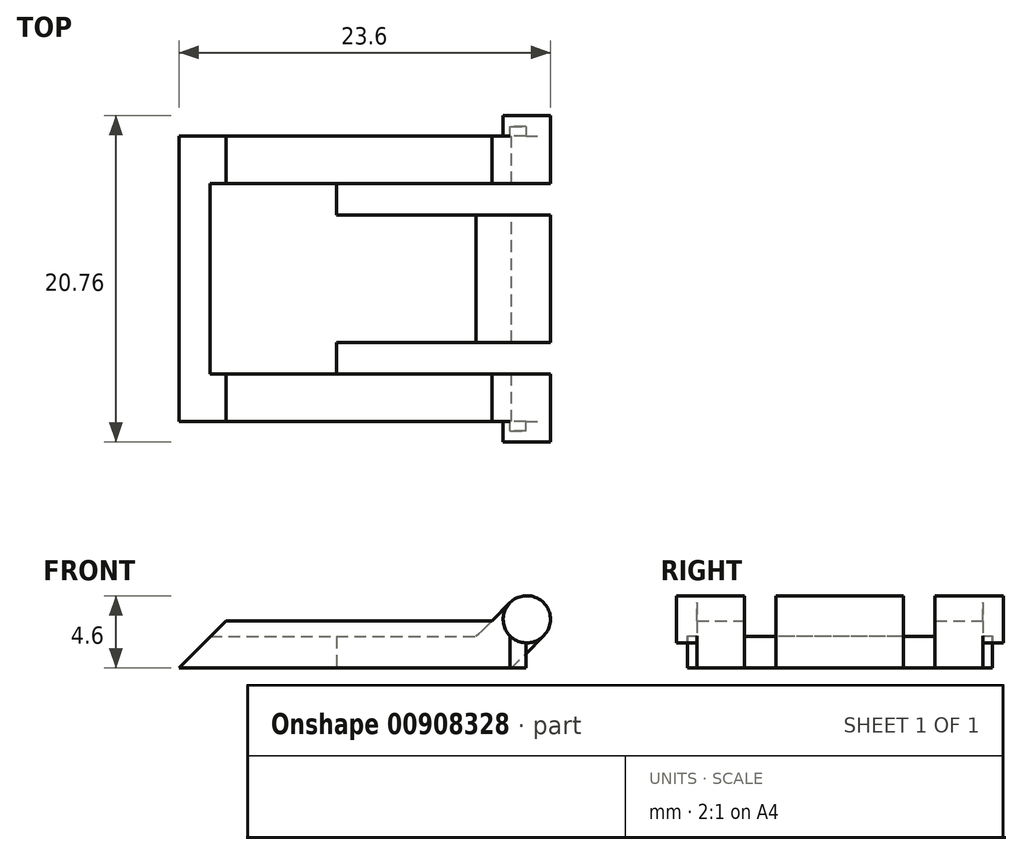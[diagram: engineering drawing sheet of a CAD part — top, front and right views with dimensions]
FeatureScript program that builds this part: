
annotation { "Feature Type Name" : "Feature", "Feature Type Description" : "" }
export const myFeature = defineFeature(function(context is Context, id is Id, definition is map)
    precondition{}
    {
        {
            var Q0;
            Q0=qCreatedBy(makeId("Front.planeOp"),FACE);
            var sketch = newSketch(context, id + "F0", { "sketchPlane" : qUnion([Q0])});
            skLineSegment(sketch, "E0", {"start": v(-6.08, 0) * mm, "end": v(15.04, 0) * mm});
            skLineSegment(sketch, "E1", {"start": v(-3.08, 3) * mm, "end": v(-6.08, 0) * mm});
            skLineSegment(sketch, "E2.trimOffspring", {"start": v(13.8, 3) * mm, "end": v(-3.08, 3) * mm});
            skArc(sketch, "E3", {"start": v(17.08, 2.04) * mm, "mid": v(17.08, 4.16) * mm, "end": v(14.96, 4.16) * mm});
            skLineSegment(sketch, "E4", {"start": v(15.04, 0) * mm, "end": v(17.08, 2.04) * mm});
            skLineSegment(sketch, "E5", {"start": v(13.8, 3) * mm, "end": v(14.96, 4.16) * mm});
            skSolve(sketch);
        }
        {
            var Q0;
            Q0 = qSketchRegion(id + "F0", true);
            extrude(context, id + "F1", {"entities" : qUnion([Q0]), "endBound" : BoundingType.SYMMETRIC, "depth" : 18.15 * mm, "offsetDistance" : 25 * mm});
        }
        {
            var Q0;
            Q0=makeQuery(id+"F1.opExtrude","CAP_FACE",FACE,{"disambiguationData":[OSD([sQuery(id+"F0.wireOp",EDGE,"E0"),sQuery(id+"F0.wireOp",EDGE,"IyzmLPVo-ZiIU-ZuMi-H74O-UJ5JQLBCPmE3"),sQuery(id+"F0.wireOp",EDGE,"E1"),sQuery(id+"F0.wireOp",EDGE,"0OPfdOSm-VN7Y-lchg-oPGg-Y34SgASty5nC"),sQuery(id+"F0.wireOp",EDGE,"E2.trimOffspring")])],"isStart":false});
            var sketch = newSketch(context, id + "F2", { "sketchPlane" : qUnion([Q0])});
            skCircle(sketch, "E6", {"center": v(16.02, 3.1) * mm, "radius": 1.5 * mm});
            skSolve(sketch);
        }
        {
            var Q0;
            {var subQ0=sQuery(id+"F2.wireOp",EDGE,"E6");var subQ1=makeQuery(id+"F2.imprint","INTERSECT",VERTEX,{"derivedFrom":[makeQuery(id+"F1.opExtrude","CAP_EDGE",EDGE,{"disambiguationData":[OSD([sQuery(id+"F0.wireOp",EDGE,"IyzmLPVo-ZiIU-ZuMi-H74O-UJ5JQLBCPmE3")])],"isStart":false}),subQ0]});Q0=makeQuery(id+"F2.imprint","IMPRINT",FACE,{"disambiguationData":[TD([[makeQuery(id+"F2.imprint","IMPRINT",EDGE,{"disambiguationData":[TD([[subQ1,-1.0]])],"derivedFrom":subQ0}),1.0]])]});}
            var Q1;
            Q1=sQuery(id+"F2.wireOp",EDGE,"E6");
            extrude(context, id + "F3", {"entities" : qUnion([Q0]), "surfaceEntities" : qUnion([Q1]), "depth" : 1.3 * mm, "offsetDistance" : 25 * mm});
        }
        {
            var Q0;
            Q0=makeQuery(id+"F3.opExtrude","SWEPT_BODY",BODY,{"disambiguationData":[OSD([sQuery(id+"F2.wireOp",EDGE,"E6")])]});
            var Q1;
            Q1=qCreatedBy(makeId("Front.planeOp"),FACE);
            mirror(context, id + "F4", {"operationType" : NewBodyOperationType.ADD, "entities" : qUnion([Q0]), "mirrorPlane" : qUnion([Q1])});
        }
        {
            var Q0;
            Q0=qCreatedBy(makeId("Front.planeOp"),FACE);
            var sketch = newSketch(context, id + "F5", { "sketchPlane" : qUnion([Q0])});
            skLineSegment(sketch, "E7.0", {"start": v(13.8, 3) * mm, "end": v(-3.08, 3) * mm});
            skLineSegment(sketch, "E7.2", {"start": v(-3.08, 3) * mm, "end": v(-4.08, 2) * mm});
            skLineSegment(sketch, "E8", {"start": v(-4.08, 2) * mm, "end": v(12.8, 2) * mm});
            skLineSegment(sketch, "E9", {"start": v(12.8, 2) * mm, "end": v(13.8, 3) * mm});
            skPoint(sketch, "E10.orphan", {"position": v(-6.08, 0) * mm});
            skSolve(sketch);
        }
        {
            var Q0;
            Q0 = qSketchRegion(id + "F5", true);
            extrude(context, id + "F6", {"entities" : qUnion([Q0]), "operationType" : NewBodyOperationType.REMOVE, "endBound" : BoundingType.SYMMETRIC, "oppositeDirection" : true, "depth" : 12.1 * mm, "offsetDistance" : 25 * mm});
        }
        {
            var Q0;
            Q0=qCreatedBy(makeId("Top.planeOp"),FACE);
            var sketch = newSketch(context, id + "F7", { "sketchPlane" : qUnion([Q0])});
            skPoint(sketch, "E11.1", {"position": v(-6.08, 0) * mm});
            skPoint(sketch, "E12.0", {"position": v(12.8, -6.05) * mm});
            skLineSegment(sketch, "E13", {"start": v(3.92, -6.05) * mm, "end": v(3.92, -4.05) * mm});
            skLineSegment(sketch, "E14", {"start": v(3.92, -4.05) * mm, "end": v(18.92, -4.05) * mm});
            skLineSegment(sketch, "E15", {"start": v(18.92, -4.05) * mm, "end": v(18.92, -6.05) * mm});
            skLineSegment(sketch, "E16", {"start": v(18.92, -6.05) * mm, "end": v(3.92, -6.05) * mm});
            skLineSegment(sketch, "E17.MirrorCS", {"start": v(18.92, 4.05) * mm, "end": v(18.92, 6.05) * mm});
            skLineSegment(sketch, "E18.MirrorCS", {"start": v(3.92, 4.05) * mm, "end": v(18.92, 4.05) * mm});
            skLineSegment(sketch, "E19.MirrorCS", {"start": v(18.92, 6.05) * mm, "end": v(3.92, 6.05) * mm});
            skLineSegment(sketch, "E20.MirrorCS", {"start": v(3.92, 6.05) * mm, "end": v(3.92, 4.05) * mm});
            skSolve(sketch);
        }
        {
            var Q0;
            Q0=makeQuery(id+"F7.imprint","IMPRINT",FACE,{"disambiguationData":[TD([[makeQuery(id+"F7.imprint","IMPRINT",EDGE,{"derivedFrom":sQuery(id+"F7.wireOp",EDGE,"E13")}),-1.0]])]});
            var Q1;
            Q1=makeQuery(id+"F7.imprint","IMPRINT",FACE,{"disambiguationData":[TD([[makeQuery(id+"F7.imprint","IMPRINT",EDGE,{"derivedFrom":sQuery(id+"F7.wireOp",EDGE,"E17.MirrorCS")}),1.0]])]});
            extrude(context, id + "F8", {"entities" : qUnion([Q0, Q1]), "operationType" : NewBodyOperationType.REMOVE, "endBound" : BoundingType.THROUGH_ALL, "depth" : 25 * mm, "offsetDistance" : 25 * mm});
        }
        {
            var Q0;
            Q0=qCreatedBy(makeId("Top.planeOp"),FACE);
            var sketch = newSketch(context, id + "F9", { "sketchPlane" : qUnion([Q0])});
            skPoint(sketch, "E21.0", {"position": v(14.96, 9.07) * mm});
            skLineSegment(sketch, "E22", {"start": v(14.96, 9.07) * mm, "end": v(14.96, 9.67) * mm});
            skLineSegment(sketch, "E23", {"start": v(14.96, 9.67) * mm, "end": v(15.96, 9.67) * mm});
            skLineSegment(sketch, "E24", {"start": v(15.96, 9.67) * mm, "end": v(15.96, 9.07) * mm});
            skLineSegment(sketch, "E25", {"start": v(15.96, 9.07) * mm, "end": v(14.96, 9.07) * mm});
            skLineSegment(sketch, "E26.MirrorCS", {"start": v(15.96, -9.67) * mm, "end": v(15.96, -9.07) * mm});
            skLineSegment(sketch, "E27.MirrorCS", {"start": v(14.96, -9.67) * mm, "end": v(15.96, -9.67) * mm});
            skLineSegment(sketch, "E28.MirrorCS", {"start": v(14.96, -9.07) * mm, "end": v(14.96, -9.67) * mm});
            skLineSegment(sketch, "E29.MirrorCS", {"start": v(15.96, -9.07) * mm, "end": v(14.96, -9.07) * mm});
            skSolve(sketch);
        }
        {
            var Q0;
            Q0 = qSketchRegion(id + "F9", true);
            extrude(context, id + "F10", {"entities" : qUnion([Q0]), "operationType" : NewBodyOperationType.ADD, "depth" : 3 * mm, "offsetDistance" : 25 * mm});
        }
    });
